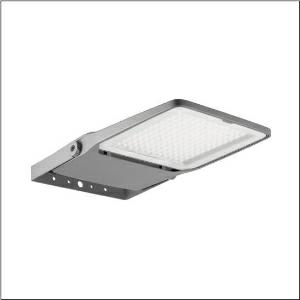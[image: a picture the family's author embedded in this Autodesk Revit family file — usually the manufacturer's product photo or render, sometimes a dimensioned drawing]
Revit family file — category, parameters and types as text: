
# Revit family: floodlight_fl_20_midi___rs17_5xa7682e1b2ac_1478
name_source: partatom
category: Lighting Fixtures
units: mm (PartAtom-declared; Revit-internal decimal feet)

## family parameters
Cut with Voids When Loaded = No
Host = Face
Light Source = No
Part Type = Normal
Room Calculation Point = No
Round Connector Dimension = Use Diameter
Shared = No

## types (1)
- --- (1 x LED 3000K / CRI = 80 (unbekannt), 22840 lm, 3000K)
    Apparent Load = 208 VA
    CIE Flux Codes = 79 92 99 100 100
    Color Rendering = 80
    Color Temperature = 3000K
    Default Elevation = 1800 mm
    Description = Floodlight FL 20 midi, floodlight, primary light control with lens, of plastic, primary optical cover: protective disc, of toughened safety glass, transparent, light distribution: RS17, light emission: direct distribution, primary light characteristic: rotationally symmetric, installation type: surface-mounted, LED High Power LED, rated luminous flux: 22.840 lm, light colour: 830, colour temperature: 3000K, control gear: ECG Plus, control: flexible luminous flux parameterisation, time-dependent luminous flux control, digital communication interface, power reduction, overheat protection, electronic power reduction, with terminal, 5-pole, max. 2.5mm², mains connection: 220..240V, AC, 50/60Hz, rated input power: 208W, LED unit, of diecast aluminium, powder-coated, Siteco® metallic grey (DB 702S), length: 731 mm, width: 450 mm, height: 76mm, housing frame, of diecast aluminium, powder-coated, Siteco® metallic grey (DB 702S), wall fastening, of steel, powder-coated, Siteco® metallic grey (DB 702S), DALIprotection rating (complete): IP66, insulation class (complete): insulation class II (safety insulation), certification: CE, ENEC, VDE, protection symbol: D, permissible ambient temperature for indoor applications: -40..+40°C, permissible ambient temperature for outdoor applications: -40..+50°C, standard: DIN EN 12944, packaging unit: 1 piece

Light Distribution: RS17
    Height = 76 mm
    Lamp = 1 x LED 3000K / CRI >= 80 (unbekannt)
    Lamp Light Flux = 22840 lm
    Lamp count = 1
    Length = 731 mm
    Luminous efficacy = 110 lm/W
    Manufacturer = Siteco
    ModVariant = No
    Model = 5XA7682E1B2AC
    Number of Poles = 1
    OnlyDefault = Yes
    Power Factor = 1
    Product Name = Floodlight FL 20 midi | RS17
    Product group = floodlight | pylon top
    ProductGroupID = 6101
    Protection Class = Protection class II
    Protection Degree = IP 66
    RLX_Detail_Level = 1
    RlxData = <blob elided: 86285 chars, md5=33314525>
    Socket = socket
    Standby Power = 0 W
    System Light Flux = 22840 lm
    System Power = 208 W
    Type Comments = factory setting: luminous flux: 100 % | dim-lin: 254 | 484 mA
    Type Image = l_1005944.jpg
    URL = http://relux.com
    VarID = @adj_141849
    Voltage = 0 V
    Weight = 0.00 kg
    Width = 450 mm

## geometry (parser evidence)
native form markers: Blend x4, Sweep x11
no freeform markers — native parametric forms only
